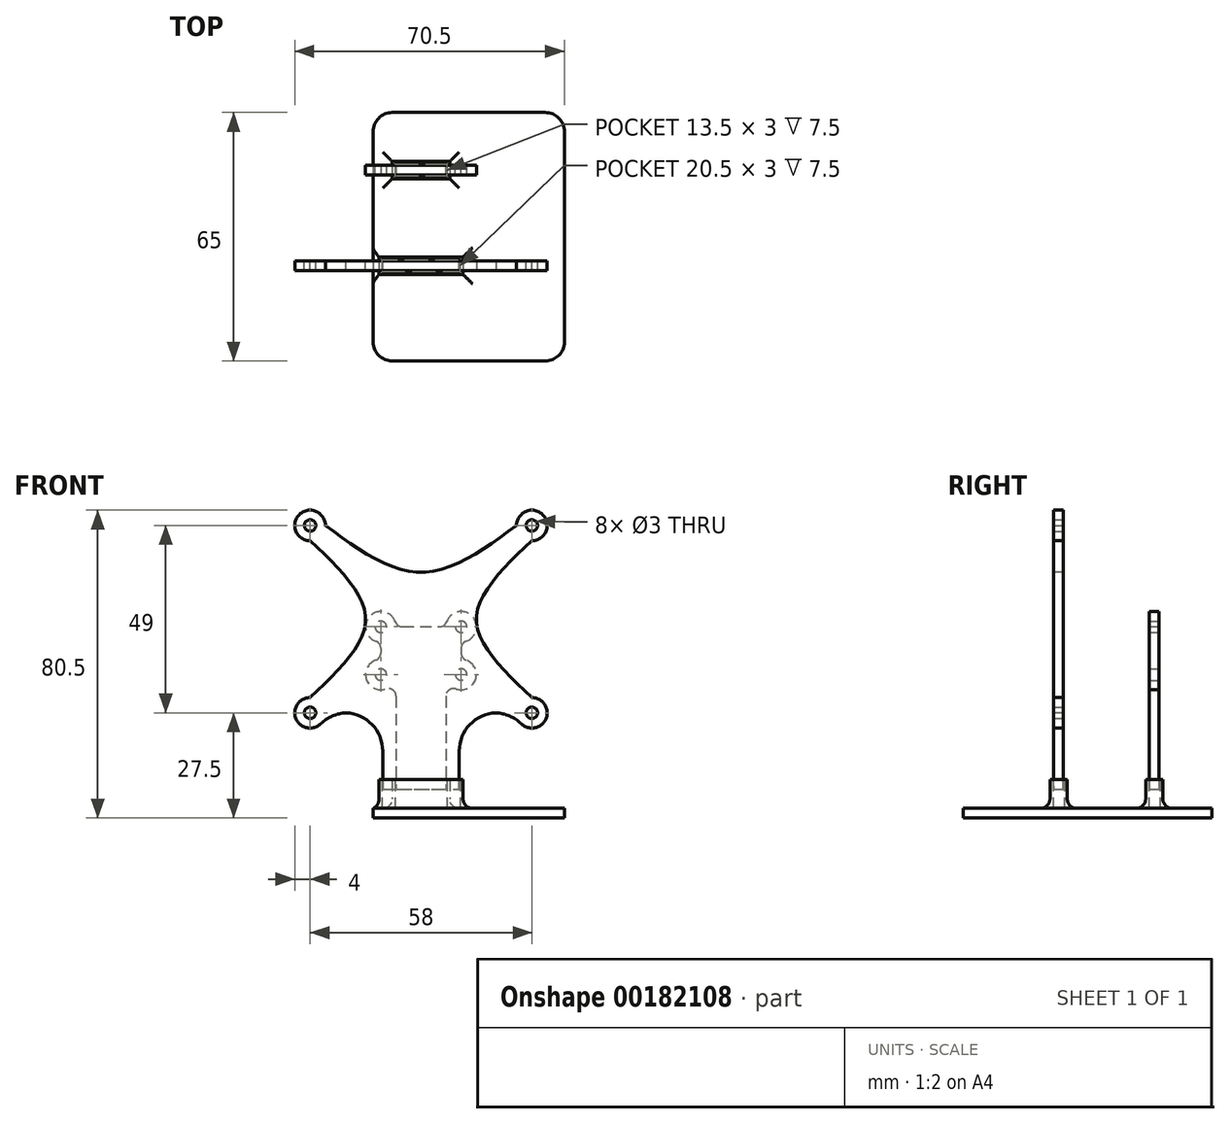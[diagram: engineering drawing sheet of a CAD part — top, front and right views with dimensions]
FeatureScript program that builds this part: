
annotation { "Feature Type Name" : "Feature", "Feature Type Description" : "" }
export const myFeature = defineFeature(function(context is Context, id is Id, definition is map)
    precondition{}
    {
        {
            var Q0;
            Q0=qCreatedBy(makeId("Front.planeOp"),FACE);
            var sketch = newSketch(context, id + "F0", { "sketchPlane" : qUnion([Q0])});
            skLineSegment(sketch, "E0.bottom", {"start": v(29, 20) * mm, "end": v(-29, 20) * mm, "construction": true});
            skLineSegment(sketch, "E0.top", {"start": v(29, 69) * mm, "end": v(-29, 69) * mm, "construction": true});
            skLineSegment(sketch, "E0.left", {"start": v(29, 20) * mm, "end": v(29, 69) * mm, "construction": true});
            skLineSegment(sketch, "E0.right", {"start": v(-29, 20) * mm, "end": v(-29, 69) * mm, "construction": true});
            skPoint(sketch, "E0.middle", {"position": v(0, 44.5) * mm});
            skCircle(sketch, "E1", {"center": v(-29, 69) * mm, "radius": 1.5 * mm});
            skCircle(sketch, "E2", {"center": v(29, 69) * mm, "radius": 1.5 * mm});
            skCircle(sketch, "E3", {"center": v(-29, 20) * mm, "radius": 1.5 * mm});
            skCircle(sketch, "E4", {"center": v(29, 20) * mm, "radius": 1.5 * mm});
            skCircle(sketch, "E5", {"center": v(-29, 69) * mm, "radius": 4 * mm});
            skCircle(sketch, "E6", {"center": v(29, 69) * mm, "radius": 4 * mm});
            skCircle(sketch, "E7", {"center": v(29, 20) * mm, "radius": 4 * mm});
            skCircle(sketch, "E8", {"center": v(-29, 20) * mm, "radius": 4 * mm});
            skLineSegment(sketch, "E9", {"start": v(0, 44.5) * mm, "end": v(-29, 44.5) * mm, "construction": true});
            skLineSegment(sketch, "E10", {"start": v(0, 44.5) * mm, "end": v(29, 44.5) * mm, "construction": true});
            skPoint(sketch, "E11", {"position": v(-14.5, 44.5) * mm});
            skPoint(sketch, "E12", {"position": v(14.5, 44.5) * mm});
            skFitSpline(sketch, "E13", {"points": [v(-29, 65) * mm, v(-14.5, 44.5) * mm, v(-29, 24) * mm], "startDerivative": vector(43.5, -41) * mm, "endDerivative": vector(-43.5, -41) * mm});
            skLineSegment(sketch, "E14", {"start": v(0, 44.5) * mm, "end": v(0, 69) * mm, "construction": true});
            skLineSegment(sketch, "E15", {"start": v(0, 44.5) * mm, "end": v(0, 20) * mm, "construction": true});
            skPoint(sketch, "E16", {"position": v(0, 56.75) * mm});
            skFitSpline(sketch, "E17", {"points": [v(-25, 69) * mm, v(0, 56.75) * mm, v(25, 69) * mm], "startDerivative": vector(50, -36.75) * mm, "endDerivative": vector(50, 36.75) * mm});
            skFitSpline(sketch, "E18", {"points": [v(29, 65) * mm, v(14.5, 44.5) * mm, v(29, 24) * mm], "startDerivative": vector(-43.5, -41) * mm, "endDerivative": vector(43.5, -41) * mm});
            skLineSegment(sketch, "E19.bottom", {"start": v(10, 20) * mm, "end": v(-10, 20) * mm, "construction": true});
            skLineSegment(sketch, "E20", {"start": v(-25, 20) * mm, "end": v(-10, 20) * mm});
            skLineSegment(sketch, "E21", {"start": v(10, 20) * mm, "end": v(25, 20) * mm});
            skLineSegment(sketch, "E22.bottom", {"start": v(-10, 20) * mm, "end": v(10, 20) * mm, "construction": true});
            skLineSegment(sketch, "E22.top", {"start": v(-10, 0) * mm, "end": v(10, 0) * mm, "construction": true});
            skLineSegment(sketch, "E22.left", {"start": v(-10, 20) * mm, "end": v(-10, 0) * mm, "construction": true});
            skLineSegment(sketch, "E22.right", {"start": v(10, 20) * mm, "end": v(10, 0) * mm, "construction": true});
            skLineSegment(sketch, "E23", {"start": v(-10, 20) * mm, "end": v(-10, 0) * mm});
            skLineSegment(sketch, "E24", {"start": v(-10, 0) * mm, "end": v(10, 0) * mm});
            skLineSegment(sketch, "E25", {"start": v(10, 0) * mm, "end": v(10, 20) * mm});
            skSolve(sketch);
        }
        {
            var Q0;
            Q0 = qSketchRegion(id + "F0", true);
            extrude(context, id + "F1", {"entities" : qUnion([Q0]), "depth" : 2.5 * mm});
        }
        {
            var Q0;
            Q0=makeQuery(id+"F1.opExtrude","SWEPT_EDGE",EDGE,{"disambiguationData":[OSD([sQuery(id+"F0.wireOp",EDGE,"E20"),sQuery(id+"F0.wireOp",EDGE,"rsNHsTDQ-MVS5-BQcW-vaOX-2bWjhTbOwRBZ")])]});
            var Q1;
            Q1=makeQuery(id+"F1.opExtrude","SWEPT_EDGE",EDGE,{"disambiguationData":[OSD([sQuery(id+"F0.wireOp",EDGE,"F6KjoTt9-LNtF-z9HA-2xc9-gbPFErhoMCAn"),sQuery(id+"F0.wireOp",EDGE,"E21")])]});
            fillet(context, id + "F2", {"entities" : qUnion([Q0, Q1]), "radius" : 10 * mm, "tangentPropagation" : true, "allowEdgeOverflow" : false});
        }
        {
            var Q0;
            Q0=qCreatedBy(makeId("Front.planeOp"),FACE);
            cPlane(context, id + "F3", {"entities" : qUnion([Q0]), "cplaneType" : CPlaneType.OFFSET, "offset" : 25 * mm, "oppositeDirection" : true, "width" : 150 * mm, "height" : 150 * mm});
        }
        {
            var Q0;
            Q0=qCreatedBy(id+"F3.planeOp",FACE);
            var sketch = newSketch(context, id + "F4", { "sketchPlane" : qUnion([Q0])});
            skLineSegment(sketch, "E26.bottom", {"start": v(10.5, 42.5) * mm, "end": v(-10.5, 42.5) * mm, "construction": true});
            skLineSegment(sketch, "E26.top", {"start": v(10.5, 30) * mm, "end": v(-10.5, 30) * mm, "construction": true});
            skLineSegment(sketch, "E26.left", {"start": v(10.5, 42.5) * mm, "end": v(10.5, 30) * mm, "construction": true});
            skLineSegment(sketch, "E26.right", {"start": v(-10.5, 42.5) * mm, "end": v(-10.5, 30) * mm, "construction": true});
            skPoint(sketch, "E26.middle", {"position": v(0, 36.25) * mm});
            skCircle(sketch, "E27", {"center": v(-10.5, 42.5) * mm, "radius": 1.5 * mm});
            skCircle(sketch, "E28", {"center": v(10.5, 42.5) * mm, "radius": 1.5 * mm});
            skCircle(sketch, "E29", {"center": v(10.5, 30) * mm, "radius": 1.5 * mm});
            skCircle(sketch, "E30", {"center": v(-10.5, 30) * mm, "radius": 1.5 * mm});
            skCircle(sketch, "E31", {"center": v(-10.5, 42.5) * mm, "radius": 4 * mm});
            skCircle(sketch, "E32", {"center": v(10.5, 42.5) * mm, "radius": 4 * mm});
            skCircle(sketch, "E33", {"center": v(10.5, 30) * mm, "radius": 4 * mm});
            skCircle(sketch, "E34", {"center": v(-10.5, 30) * mm, "radius": 4 * mm});
            skLineSegment(sketch, "E35", {"start": v(-10.5, 38.5) * mm, "end": v(-10.5, 34) * mm});
            skLineSegment(sketch, "E36", {"start": v(-6.5, 42.5) * mm, "end": v(6.5, 42.5) * mm});
            skLineSegment(sketch, "E37", {"start": v(10.5, 38.5) * mm, "end": v(10.5, 34) * mm});
            skLineSegment(sketch, "E38.bottom", {"start": v(-6.5, 30) * mm, "end": v(6.5, 30) * mm});
            skLineSegment(sketch, "E38.top", {"start": v(-6.5, 0) * mm, "end": v(6.5, 0) * mm});
            skLineSegment(sketch, "E38.left", {"start": v(-6.5, 30) * mm, "end": v(-6.5, 0) * mm});
            skLineSegment(sketch, "E38.right", {"start": v(6.5, 30) * mm, "end": v(6.5, 0) * mm});
            skSolve(sketch);
        }
        {
            var Q0;
            Q0 = qSketchRegion(id + "F4", true);
            extrude(context, id + "F5", {"entities" : qUnion([Q0]), "depth" : 2.5 * mm});
        }
        {
            var Q0;
            Q0=makeQuery(id+"F5.opExtrude","SWEPT_EDGE",EDGE,{"disambiguationData":[OSD([sQuery(id+"F4.wireOp",EDGE,"E31"),sQuery(id+"F4.wireOp",EDGE,"E36")])]});
            var Q1;
            Q1=makeQuery(id+"F5.opExtrude","SWEPT_EDGE",EDGE,{"disambiguationData":[OSD([sQuery(id+"F4.wireOp",EDGE,"E32"),sQuery(id+"F4.wireOp",EDGE,"E36")])]});
            var Q2;
            Q2=makeQuery(id+"F5.opExtrude","SWEPT_EDGE",EDGE,{"disambiguationData":[OSD([sQuery(id+"F4.wireOp",EDGE,"E32"),sQuery(id+"F4.wireOp",EDGE,"E37")])]});
            var Q3;
            Q3=makeQuery(id+"F5.opExtrude","SWEPT_EDGE",EDGE,{"disambiguationData":[OSD([sQuery(id+"F4.wireOp",EDGE,"E31"),sQuery(id+"F4.wireOp",EDGE,"E35")])]});
            var Q4;
            Q4=makeQuery(id+"F5.opExtrude","SWEPT_EDGE",EDGE,{"disambiguationData":[OSD([sQuery(id+"F4.wireOp",EDGE,"E34"),sQuery(id+"F4.wireOp",EDGE,"E35")])]});
            var Q5;
            Q5=makeQuery(id+"F5.opExtrude","SWEPT_EDGE",EDGE,{"disambiguationData":[OSD([sQuery(id+"F4.wireOp",EDGE,"E33"),sQuery(id+"F4.wireOp",EDGE,"E37")])]});
            fillet(context, id + "F6", {"entities" : qUnion([Q0, Q1, Q2, Q3, Q4, Q5]), "radius" : 2 * mm, "tangentPropagation" : true, "allowEdgeOverflow" : false});
        }
        {
            var Q0;
            Q0=makeQuery(id+"F5.opExtrude","SWEPT_EDGE",EDGE,{"disambiguationData":[OSD([sQuery(id+"F4.wireOp",EDGE,"E34"),sQuery(id+"F4.wireOp",EDGE,"E38.bottom"),sQuery(id+"F4.wireOp",EDGE,"E38.left")])]});
            var Q1;
            Q1=makeQuery(id+"F5.opExtrude","SWEPT_EDGE",EDGE,{"disambiguationData":[OSD([sQuery(id+"F4.wireOp",EDGE,"E33"),sQuery(id+"F4.wireOp",EDGE,"E38.bottom"),sQuery(id+"F4.wireOp",EDGE,"E38.right")])]});
            fillet(context, id + "F7", {"entities" : qUnion([Q0, Q1]), "radius" : 2 * mm, "tangentPropagation" : true, "allowEdgeOverflow" : false});
        }
        {
            var Q0;
            Q0=qCreatedBy(makeId("Top.planeOp"),FACE);
            cPlane(context, id + "F8", {"entities" : qUnion([Q0]), "cplaneType" : CPlaneType.OFFSET, "offset" : 5 * mm, "oppositeDirection" : true, "width" : 150 * mm, "height" : 150 * mm});
        }
        {
            var Q0;
            Q0=qCreatedBy(id+"F8.planeOp",FACE);
            var sketch = newSketch(context, id + "F9", { "sketchPlane" : qUnion([Q0])});
            skLineSegment(sketch, "E39.bottom", {"start": v(12.5, 38.85) * mm, "end": v(-12.5, 38.85) * mm});
            skLineSegment(sketch, "E39.top", {"start": v(12.5, -26.15) * mm, "end": v(-12.5, -26.15) * mm});
            skLineSegment(sketch, "E39.left", {"start": v(12.5, 38.85) * mm, "end": v(12.5, -26.15) * mm});
            skLineSegment(sketch, "E39.right", {"start": v(-12.5, 38.85) * mm, "end": v(-12.5, -26.15) * mm});
            skPoint(sketch, "E39.middle", {"position": v(0, 6.35) * mm});
            skLineSegment(sketch, "E40.bottom", {"start": v(6.75, 25.28) * mm, "end": v(-6.75, 25.28) * mm});
            skLineSegment(sketch, "E40.top", {"start": v(6.75, 22.28) * mm, "end": v(-6.75, 22.28) * mm});
            skLineSegment(sketch, "E40.left", {"start": v(6.75, 25.28) * mm, "end": v(6.75, 22.28) * mm});
            skLineSegment(sketch, "E40.right", {"start": v(-6.75, 25.28) * mm, "end": v(-6.75, 22.28) * mm});
            skPoint(sketch, "E40.middle", {"position": v(0, 23.78) * mm});
            skLineSegment(sketch, "E41.0", {"start": v(7.5, 21.53) * mm, "end": v(-7.5, 21.53) * mm});
            skLineSegment(sketch, "E41.1", {"start": v(7.5, 26.03) * mm, "end": v(7.5, 21.53) * mm});
            skLineSegment(sketch, "E41.2", {"start": v(7.5, 26.03) * mm, "end": v(-7.5, 26.03) * mm});
            skLineSegment(sketch, "E41.3", {"start": v(-7.5, 26.03) * mm, "end": v(-7.5, 21.53) * mm});
            skLineSegment(sketch, "E42.bottom", {"start": v(10.25, 0.26) * mm, "end": v(-10.25, 0.26) * mm});
            skLineSegment(sketch, "E42.top", {"start": v(10.25, -2.74) * mm, "end": v(-10.25, -2.74) * mm});
            skLineSegment(sketch, "E42.left", {"start": v(10.25, 0.26) * mm, "end": v(10.25, -2.74) * mm});
            skLineSegment(sketch, "E42.right", {"start": v(-10.25, 0.26) * mm, "end": v(-10.25, -2.74) * mm});
            skPoint(sketch, "E42.middle", {"position": v(0, -1.24) * mm});
            skLineSegment(sketch, "E43.0", {"start": v(11, -3.49) * mm, "end": v(-11, -3.49) * mm});
            skLineSegment(sketch, "E43.1", {"start": v(11, 1.01) * mm, "end": v(11, -3.49) * mm});
            skLineSegment(sketch, "E43.2", {"start": v(11, 1.01) * mm, "end": v(-11, 1.01) * mm});
            skLineSegment(sketch, "E43.3", {"start": v(-11, 1.01) * mm, "end": v(-11, -3.49) * mm});
            skLineSegment(sketch, "E44.bottom", {"start": v(12.5, 38.85) * mm, "end": v(37.5, 38.85) * mm});
            skLineSegment(sketch, "E44.top", {"start": v(12.5, -26.15) * mm, "end": v(37.5, -26.15) * mm});
            skLineSegment(sketch, "E44.right", {"start": v(37.5, 38.85) * mm, "end": v(37.5, -26.15) * mm});
            skSolve(sketch);
        }
        {
            var Q0;
            Q0 = qSketchRegion(id + "F9", true);
            var Q1;
            Q1=makeQuery(id+"F9.imprint","IMPRINT",FACE,{"disambiguationData":[TD([[makeQuery(id+"F9.imprint","IMPRINT",EDGE,{"derivedFrom":sQuery(id+"F9.wireOp",EDGE,"E40.bottom")}),1.0]])]});
            var Q2;
            Q2=makeQuery(id+"F9.imprint","IMPRINT",FACE,{"disambiguationData":[TD([[makeQuery(id+"F9.imprint","IMPRINT",EDGE,{"derivedFrom":sQuery(id+"F9.wireOp",EDGE,"E40.bottom")}),-1.0]])]});
            var Q3;
            Q3=makeQuery(id+"F9.imprint","IMPRINT",FACE,{"disambiguationData":[TD([[makeQuery(id+"F9.imprint","IMPRINT",EDGE,{"derivedFrom":sQuery(id+"F9.wireOp",EDGE,"E42.bottom")}),-1.0]])]});
            var Q4;
            Q4=makeQuery(id+"F9.imprint","IMPRINT",FACE,{"disambiguationData":[TD([[makeQuery(id+"F9.imprint","IMPRINT",EDGE,{"derivedFrom":sQuery(id+"F9.wireOp",EDGE,"E42.bottom")}),1.0]])]});
            extrude(context, id + "F10", {"entities" : qUnion([Q0, Q1, Q2, Q3, Q4]), "oppositeDirection" : true, "depth" : 2.5 * mm});
        }
        {
            var Q0;
            Q0=makeQuery(id+"F9.imprint","IMPRINT",FACE,{"disambiguationData":[TD([[makeQuery(id+"F9.imprint","IMPRINT",EDGE,{"derivedFrom":sQuery(id+"F9.wireOp",EDGE,"E40.bottom")}),-1.0]])]});
            var Q1;
            Q1=makeQuery(id+"F9.imprint","IMPRINT",FACE,{"disambiguationData":[TD([[makeQuery(id+"F9.imprint","IMPRINT",EDGE,{"derivedFrom":sQuery(id+"F9.wireOp",EDGE,"E42.bottom")}),-1.0]])]});
            extrude(context, id + "F11", {"entities" : qUnion([Q0, Q1]), "operationType" : NewBodyOperationType.ADD, "depth" : 7.5 * mm});
        }
        {
            var Q0;
            Q0=makeQuery(id+"F10.opExtrude","SWEPT_EDGE",EDGE,{"disambiguationData":[OSD([sQuery(id+"F9.wireOp",EDGE,"E39.bottom"),sQuery(id+"F9.wireOp",EDGE,"E39.right")])]});
            var Q1;
            Q1=makeQuery(id+"F10.opExtrude","SWEPT_EDGE",EDGE,{"disambiguationData":[OSD([sQuery(id+"F9.wireOp",EDGE,"E39.top"),sQuery(id+"F9.wireOp",EDGE,"E39.right")])]});
            var Q2;
            Q2=makeQuery(id+"F10.opExtrude","SWEPT_EDGE",EDGE,{"disambiguationData":[OSD([sQuery(id+"F9.wireOp",EDGE,"E44.top"),sQuery(id+"F9.wireOp",EDGE,"E44.right")])]});
            var Q3;
            Q3=makeQuery(id+"F10.opExtrude","SWEPT_EDGE",EDGE,{"disambiguationData":[OSD([sQuery(id+"F9.wireOp",EDGE,"E44.bottom"),sQuery(id+"F9.wireOp",EDGE,"E44.right")])]});
            fillet(context, id + "F12", {"entities" : qUnion([Q0, Q1, Q2, Q3]), "radius" : 5 * mm, "tangentPropagation" : true, "allowEdgeOverflow" : false});
        }
        {
            var Q0;
            Q0=makeQuery(id+"F11.opExtrude","CAP_EDGE",EDGE,{"disambiguationData":[OSD([sQuery(id+"F9.wireOp",EDGE,"E41.2")])],"isStart":true});
            var Q1;
            Q1=makeQuery(id+"F11.opExtrude","CAP_EDGE",EDGE,{"disambiguationData":[OSD([sQuery(id+"F9.wireOp",EDGE,"E43.2")])],"isStart":true});
            var Q2;
            Q2=makeQuery(id+"F11.opExtrude","CAP_EDGE",EDGE,{"disambiguationData":[OSD([sQuery(id+"F9.wireOp",EDGE,"E41.3")])],"isStart":true});
            var Q3;
            Q3=makeQuery(id+"F11.opExtrude","CAP_EDGE",EDGE,{"disambiguationData":[OSD([sQuery(id+"F9.wireOp",EDGE,"E43.3")])],"isStart":true});
            var Q4;
            Q4=makeQuery(id+"F11.opExtrude","CAP_EDGE",EDGE,{"disambiguationData":[OSD([sQuery(id+"F9.wireOp",EDGE,"E41.0")])],"isStart":true});
            var Q5;
            Q5=makeQuery(id+"F11.opExtrude","CAP_EDGE",EDGE,{"disambiguationData":[OSD([sQuery(id+"F9.wireOp",EDGE,"E43.0")])],"isStart":true});
            var Q6;
            Q6=makeQuery(id+"F11.opExtrude","CAP_EDGE",EDGE,{"disambiguationData":[OSD([sQuery(id+"F9.wireOp",EDGE,"E41.1")])],"isStart":true});
            var Q7;
            Q7=makeQuery(id+"F11.opExtrude","CAP_EDGE",EDGE,{"disambiguationData":[OSD([sQuery(id+"F9.wireOp",EDGE,"E43.1")])],"isStart":true});
            fillet(context, id + "F13", {"entities" : qUnion([Q0, Q1, Q2, Q3, Q4, Q5, Q6, Q7]), "radius" : 2.5 * mm, "tangentPropagation" : true, "allowEdgeOverflow" : false});
        }
    });
